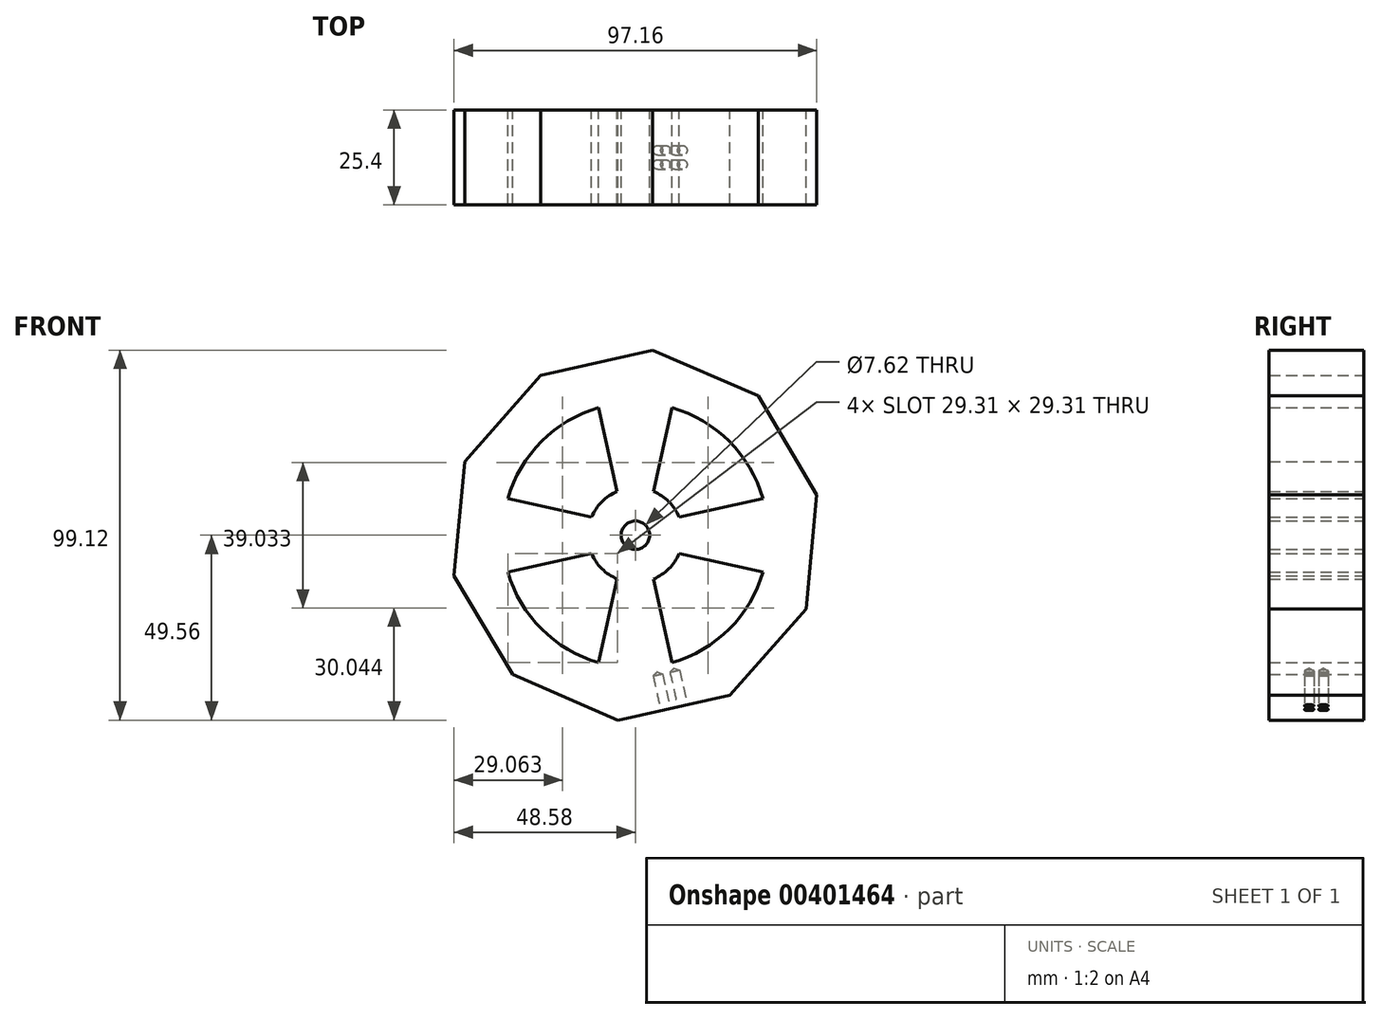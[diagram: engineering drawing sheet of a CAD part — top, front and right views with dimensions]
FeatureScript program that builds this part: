
annotation { "Feature Type Name" : "Feature", "Feature Type Description" : "" }
export const myFeature = defineFeature(function(context is Context, id is Id, definition is map)
    precondition{}
    {
        {
            var Q0;
            Q0=qCreatedBy(makeId("Front.planeOp"),FACE);
            var sketch = newSketch(context, id + "F0", { "sketchPlane" : qUnion([Q0])});
            skCircle(sketch, "E0", {"center": v(0, 0) * mm, "radius": 35.56 * mm});
            skCircle(sketch, "E1", {"center": v(0, 0) * mm, "radius": 12.7 * mm});
            skLineSegment(sketch, "E2", {"start": v(-4.86, 11.73) * mm, "end": v(-9.83, 34.17) * mm});
            skLineSegment(sketch, "E3", {"start": v(4.86, 11.73) * mm, "end": v(9.83, 34.17) * mm});
            skLineSegment(sketch, "E4", {"start": v(-11.73, 4.86) * mm, "end": v(-34.17, 9.83) * mm});
            skLineSegment(sketch, "E5", {"start": v(-11.73, -4.86) * mm, "end": v(-34.17, -9.83) * mm});
            skLineSegment(sketch, "E6", {"start": v(4.86, -11.73) * mm, "end": v(9.83, -34.17) * mm});
            skLineSegment(sketch, "E7", {"start": v(-4.86, -11.73) * mm, "end": v(-9.83, -34.17) * mm});
            skLineSegment(sketch, "E8", {"start": v(11.73, 4.86) * mm, "end": v(34.17, 9.83) * mm});
            skLineSegment(sketch, "E9", {"start": v(11.73, -4.86) * mm, "end": v(34.17, -9.83) * mm});
            skCircle(sketch, "E10", {"center": v(0, 0) * mm, "radius": 3.81 * mm});
            skLineSegment(sketch, "E11", {"start": v(0, 0) * mm, "end": v(3.5, -1.51) * mm});
            skLineSegment(sketch, "E12", {"start": v(0, 0) * mm, "end": v(1.94, -3.28) * mm});
            skLineSegment(sketch, "E13", {"start": v(0, 0) * mm, "end": v(3.72, 0.83) * mm});
            skLineSegment(sketch, "E14", {"start": v(0, 0) * mm, "end": v(2.52, 2.86) * mm});
            skLineSegment(sketch, "E15", {"start": v(0, 0) * mm, "end": v(0.36, 3.8) * mm});
            skLineSegment(sketch, "E16", {"start": v(0, 0) * mm, "end": v(-1.94, 3.28) * mm});
            skLineSegment(sketch, "E17", {"start": v(0, 0) * mm, "end": v(-3.5, 1.51) * mm});
            skLineSegment(sketch, "E18", {"start": v(0, 0) * mm, "end": v(-3.72, -0.83) * mm});
            skLineSegment(sketch, "E19", {"start": v(0, 0) * mm, "end": v(-2.52, -2.86) * mm});
            skLineSegment(sketch, "E20", {"start": v(0, 0) * mm, "end": v(-0.36, -3.8) * mm});
            skLineSegment(sketch, "E21", {"start": v(25.36, -42.84) * mm, "end": v(-4.67, -49.56) * mm});
            skLineSegment(sketch, "E22", {"start": v(-4.67, -49.56) * mm, "end": v(-32.9, -37.36) * mm});
            skLineSegment(sketch, "E23", {"start": v(-32.9, -37.36) * mm, "end": v(-48.58, -10.88) * mm});
            skLineSegment(sketch, "E24", {"start": v(-45.7, 19.75) * mm, "end": v(-48.58, -10.88) * mm});
            skLineSegment(sketch, "E25", {"start": v(-25.36, 42.84) * mm, "end": v(-45.7, 19.75) * mm});
            skLineSegment(sketch, "E26", {"start": v(4.67, 49.56) * mm, "end": v(-25.36, 42.84) * mm});
            skLineSegment(sketch, "E27", {"start": v(32.9, 37.36) * mm, "end": v(4.67, 49.56) * mm});
            skLineSegment(sketch, "E28", {"start": v(32.9, 37.36) * mm, "end": v(48.58, 10.88) * mm});
            skLineSegment(sketch, "E29", {"start": v(48.58, 10.88) * mm, "end": v(45.7, -19.75) * mm});
            skLineSegment(sketch, "E30", {"start": v(45.7, -19.75) * mm, "end": v(25.36, -42.84) * mm});
            skLineSegment(sketch, "E31.trimOffspring", {"start": v(-18.11, 30.6) * mm, "end": v(-25.36, 42.84) * mm});
            skLineSegment(sketch, "E32.trimOffspring", {"start": v(3.33, 35.4) * mm, "end": v(4.67, 49.56) * mm});
            skLineSegment(sketch, "E33.trimOffspring", {"start": v(23.5, 26.68) * mm, "end": v(32.9, 37.36) * mm});
            skLineSegment(sketch, "E34.trimOffspring", {"start": v(-32.64, 14.1) * mm, "end": v(-45.7, 19.75) * mm});
            skLineSegment(sketch, "E35.trimOffspring", {"start": v(-34.7, -7.77) * mm, "end": v(-48.58, -10.88) * mm});
            skLineSegment(sketch, "E36.trimOffspring", {"start": v(-23.5, -26.68) * mm, "end": v(-32.9, -37.36) * mm});
            skLineSegment(sketch, "E37.trimOffspring", {"start": v(-3.33, -35.4) * mm, "end": v(-4.67, -49.56) * mm});
            skLineSegment(sketch, "E38.trimOffspring", {"start": v(18.11, -30.6) * mm, "end": v(25.36, -42.84) * mm});
            skLineSegment(sketch, "E39.trimOffspring", {"start": v(32.64, -14.1) * mm, "end": v(45.7, -19.75) * mm});
            skLineSegment(sketch, "E40.trimOffspring", {"start": v(34.7, 7.77) * mm, "end": v(48.58, 10.88) * mm});
            skSolve(sketch);
        }
        {
            var Q0;
            {var subQ0=sQuery(id+"F0.wireOp",EDGE,"E1");var subQ10=makeQuery(id+"F0.imprint","INTERSECT",VERTEX,{"derivedFrom":[subQ0,sQuery(id+"F0.wireOp",EDGE,"E3")]});Q0=makeQuery(id+"F0.imprint","IMPRINT",FACE,{"disambiguationData":[TD([[makeQuery(id+"F0.imprint","IMPRINT",EDGE,{"disambiguationData":[TD([[subQ10,1.0]])],"derivedFrom":subQ0}),1.0]])]});}
            var Q1;
            {var subQ0=sQuery(id+"F0.wireOp",EDGE,"E2");Q1=makeQuery(id+"F0.imprint","IMPRINT",FACE,{"disambiguationData":[TD([[makeQuery(id+"F0.imprint","IMPRINT",EDGE,{"derivedFrom":subQ0}),-1.0]])]});}
            var Q2;
            {var subQ0=sQuery(id+"F0.wireOp",EDGE,"E8");Q2=makeQuery(id+"F0.imprint","IMPRINT",FACE,{"disambiguationData":[TD([[makeQuery(id+"F0.imprint","IMPRINT",EDGE,{"derivedFrom":subQ0}),-1.0]])]});}
            var Q3;
            {var subQ0=sQuery(id+"F0.wireOp",EDGE,"E6");Q3=makeQuery(id+"F0.imprint","IMPRINT",FACE,{"disambiguationData":[TD([[makeQuery(id+"F0.imprint","IMPRINT",EDGE,{"derivedFrom":subQ0}),-1.0]])]});}
            var Q4;
            {var subQ0=sQuery(id+"F0.wireOp",EDGE,"E4");Q4=makeQuery(id+"F0.imprint","IMPRINT",FACE,{"disambiguationData":[TD([[makeQuery(id+"F0.imprint","IMPRINT",EDGE,{"derivedFrom":subQ0}),1.0]])]});}
            var Q5;
            Q5=makeQuery(id+"F0.imprint","IMPRINT",FACE,{"disambiguationData":[TD([[makeQuery(id+"F0.imprint","IMPRINT",EDGE,{"derivedFrom":sQuery(id+"F0.wireOp",EDGE,"E24")}),1.0]])]});
            var Q6;
            Q6=makeQuery(id+"F0.imprint","IMPRINT",FACE,{"disambiguationData":[TD([[makeQuery(id+"F0.imprint","IMPRINT",EDGE,{"derivedFrom":sQuery(id+"F0.wireOp",EDGE,"E25")}),1.0]])]});
            var Q7;
            Q7=makeQuery(id+"F0.imprint","IMPRINT",FACE,{"disambiguationData":[TD([[makeQuery(id+"F0.imprint","IMPRINT",EDGE,{"derivedFrom":sQuery(id+"F0.wireOp",EDGE,"E26")}),1.0]])]});
            var Q8;
            Q8=makeQuery(id+"F0.imprint","IMPRINT",FACE,{"disambiguationData":[TD([[makeQuery(id+"F0.imprint","IMPRINT",EDGE,{"derivedFrom":sQuery(id+"F0.wireOp",EDGE,"E27")}),1.0]])]});
            var Q9;
            Q9=makeQuery(id+"F0.imprint","IMPRINT",FACE,{"disambiguationData":[TD([[makeQuery(id+"F0.imprint","IMPRINT",EDGE,{"derivedFrom":sQuery(id+"F0.wireOp",EDGE,"E28")}),-1.0]])]});
            var Q10;
            Q10=makeQuery(id+"F0.imprint","IMPRINT",FACE,{"disambiguationData":[TD([[makeQuery(id+"F0.imprint","IMPRINT",EDGE,{"derivedFrom":sQuery(id+"F0.wireOp",EDGE,"E29")}),-1.0]])]});
            var Q11;
            Q11=makeQuery(id+"F0.imprint","IMPRINT",FACE,{"disambiguationData":[TD([[makeQuery(id+"F0.imprint","IMPRINT",EDGE,{"derivedFrom":sQuery(id+"F0.wireOp",EDGE,"E30")}),-1.0]])]});
            var Q12;
            Q12=makeQuery(id+"F0.imprint","IMPRINT",FACE,{"disambiguationData":[TD([[makeQuery(id+"F0.imprint","IMPRINT",EDGE,{"derivedFrom":sQuery(id+"F0.wireOp",EDGE,"E21")}),-1.0]])]});
            var Q13;
            Q13=makeQuery(id+"F0.imprint","IMPRINT",FACE,{"disambiguationData":[TD([[makeQuery(id+"F0.imprint","IMPRINT",EDGE,{"derivedFrom":sQuery(id+"F0.wireOp",EDGE,"E22")}),-1.0]])]});
            var Q14;
            Q14=makeQuery(id+"F0.imprint","IMPRINT",FACE,{"disambiguationData":[TD([[makeQuery(id+"F0.imprint","IMPRINT",EDGE,{"derivedFrom":sQuery(id+"F0.wireOp",EDGE,"E23")}),-1.0]])]});
            extrude(context, id + "F1", {"entities" : qUnion([Q0, Q1, Q2, Q3, Q4, Q5, Q6, Q7, Q8, Q9, Q10, Q11, Q12, Q13, Q14]), "depth" : 25.4 * mm});
        }
        {
            var Q0;
            Q0=makeQuery(id+"F1.opExtrude","SWEPT_FACE",FACE,{"disambiguationData":[OSD([sQuery(id+"F0.wireOp",EDGE,"E21")])]});
            var sketch = newSketch(context, id + "F2", { "sketchPlane" : qUnion([Q0])});
            skPoint(sketch, "E41", {"position": v(-15.38, 25.4) * mm});
            skPoint(sketch, "E42", {"position": v(15.38, 25.4) * mm});
            skPoint(sketch, "E43", {"position": v(15.38, 0) * mm});
            skPoint(sketch, "E44", {"position": v(-15.38, 0) * mm});
            skLineSegment(sketch, "E45", {"start": v(-15.38, 25.4) * mm, "end": v(15.38, 0) * mm});
            skLineSegment(sketch, "E46", {"start": v(15.38, 25.4) * mm, "end": v(-15.38, 0) * mm});
            skPoint(sketch, "E47", {"position": v(-2.31, 14.6) * mm});
            skPoint(sketch, "E48", {"position": v(-2.31, 10.8) * mm});
            skPoint(sketch, "E49", {"position": v(2.31, 14.6) * mm});
            skPoint(sketch, "E50", {"position": v(2.31, 10.8) * mm});
            skPoint(sketch, "E51", {"position": v(0, 12.7) * mm});
            skSolve(sketch);
        }
        {
            var Q0;
            Q0=sQuery(id+"F2.wireOp",VERTEX,"E47");
            var Q1;
            Q1=sQuery(id+"F2.wireOp",VERTEX,"E49");
            var Q2;
            Q2=sQuery(id+"F2.wireOp",VERTEX,"E50");
            var Q3;
            Q3=sQuery(id+"F2.wireOp",VERTEX,"E48");
            var Q4;
            Q4=makeQuery(id+"F1.opExtrude","SWEPT_BODY",BODY,{"disambiguationData":[OSD([sQuery(id+"F0.wireOp",EDGE,"E0"),sQuery(id+"F0.wireOp",EDGE,"E1"),sQuery(id+"F0.wireOp",EDGE,"E2"),sQuery(id+"F0.wireOp",EDGE,"E3"),sQuery(id+"F0.wireOp",EDGE,"E4"),sQuery(id+"F0.wireOp",EDGE,"E5"),sQuery(id+"F0.wireOp",EDGE,"E6"),sQuery(id+"F0.wireOp",EDGE,"E7"),sQuery(id+"F0.wireOp",EDGE,"E8"),sQuery(id+"F0.wireOp",EDGE,"E9"),sQuery(id+"F0.wireOp",EDGE,"E10"),sQuery(id+"F0.wireOp",EDGE,"E21"),sQuery(id+"F0.wireOp",EDGE,"E22"),sQuery(id+"F0.wireOp",EDGE,"E23"),sQuery(id+"F0.wireOp",EDGE,"E24"),sQuery(id+"F0.wireOp",EDGE,"E25"),sQuery(id+"F0.wireOp",EDGE,"E26"),sQuery(id+"F0.wireOp",EDGE,"E27"),sQuery(id+"F0.wireOp",EDGE,"E28"),sQuery(id+"F0.wireOp",EDGE,"E29"),sQuery(id+"F0.wireOp",EDGE,"E30")])]});
            hole(context, id + "F3", {"style" : HoleStyle.SIMPLE, "endStyle" : HoleEndStyle.BLIND, "holeDiameter" : 2.6 * mm, "holeDepth" : 9.5 * mm, "isTappedThrough" : true, "tappedDepth" : 12.7 * mm, "tapClearance" : 3, "locations" : qUnion([Q0, Q1, Q2, Q3]), "scope" : qUnion([Q4])});
        }
    });
